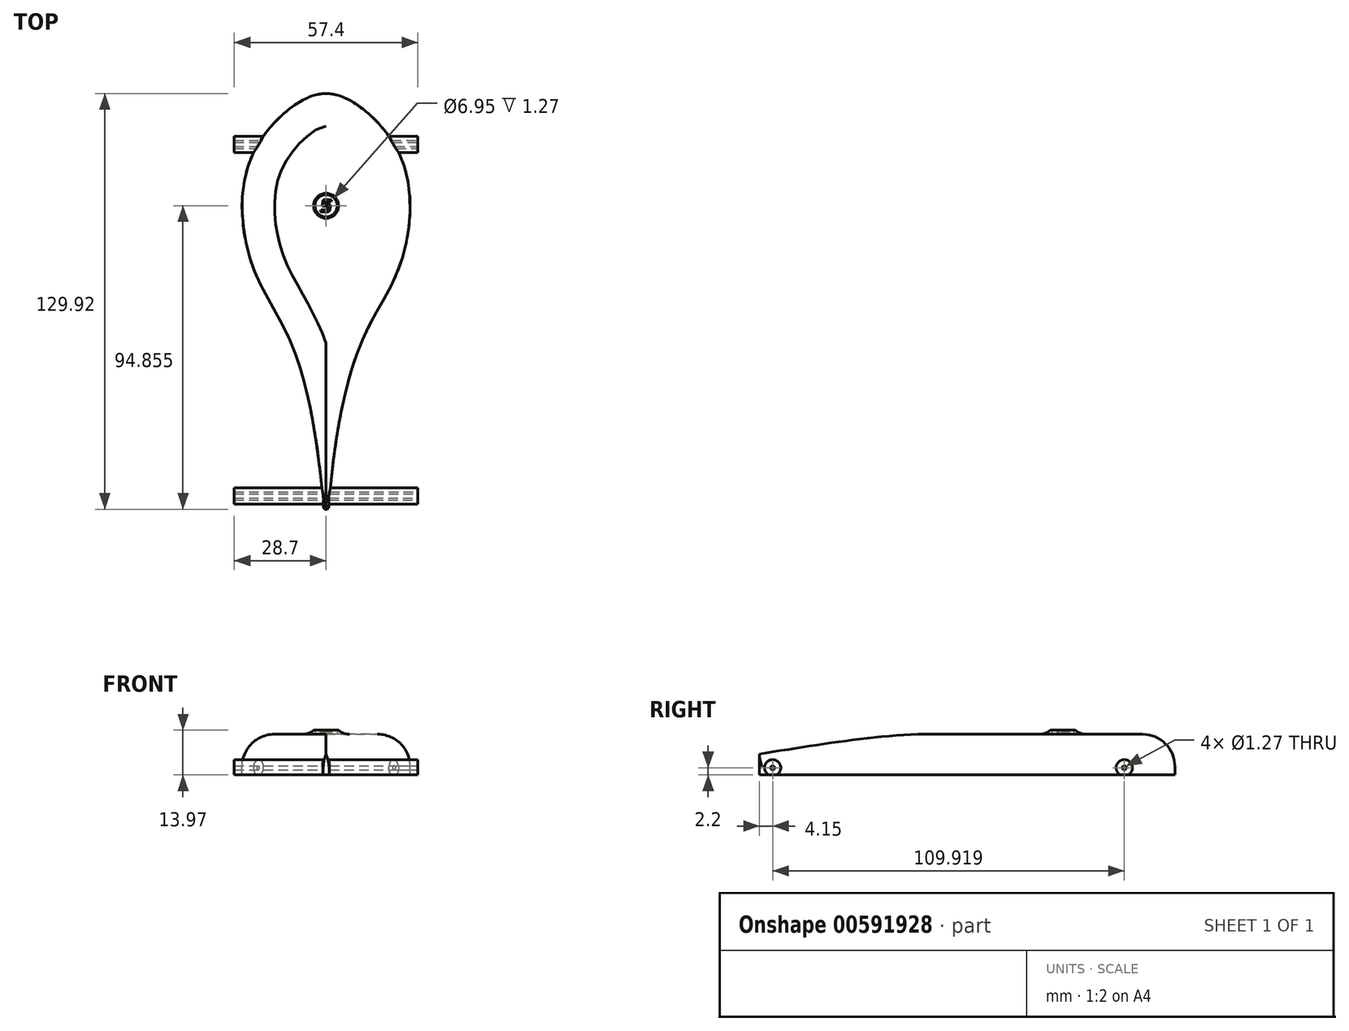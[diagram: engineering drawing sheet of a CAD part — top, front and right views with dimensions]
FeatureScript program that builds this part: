
annotation { "Feature Type Name" : "Feature", "Feature Type Description" : "" }
export const myFeature = defineFeature(function(context is Context, id is Id, definition is map)
    precondition{}
    {
        {
            var Q0;
            Q0=qCreatedBy(makeId("Top.planeOp"),FACE);
            var sketch = newSketch(context, id + "F0", { "sketchPlane" : qUnion([Q0])});
            skLineSegment(sketch, "E0", {"start": v(0, 41.15) * mm, "end": v(0, 41.15) * mm});
            skFitSpline(sketch, "E1", {"points": [v(0, 41.15) * mm, v(-11.67, 36.2) * mm, v(-24.8, 17.18) * mm, v(-22.86, -13.1) * mm, v(-9.97, -39.25) * mm, v(0, -110) * mm], "startDerivative": vector(-88.12, 0) * mm, "endDerivative": vector(1.08, -257.24) * mm});
            skLineSegment(sketch, "E2", {"start": v(0, -88.77) * mm, "end": v(0, 41.15) * mm});
            skArc(sketch, "E3", {"start": v(-0.85, -87.98) * mm, "mid": v(-0.58, -88.54) * mm, "end": v(0, -88.77) * mm});
            skSolve(sketch);
        }
        {
            var Q0;
            Q0=qSketchRegion(id+"F0",true);
            extrude(context, id + "F1", {"entities" : qUnion([Q0]), "depth" : 12.7 * mm, "offsetDistance" : 25.4 * mm});
        }
        {
            var Q0;
            Q0=qCreatedBy(makeId("Right.planeOp"),FACE);
            var sketch = newSketch(context, id + "F2", { "sketchPlane" : qUnion([Q0])});
            skArc(sketch, "E4", {"start": v(-83.35, 0) * mm, "mid": v(-84.62, 4.74) * mm, "end": v(-85.89, 0) * mm});
            skCircle(sketch, "E5", {"center": v(-84.62, 2.2) * mm, "radius": 0.64 * mm});
            skLineSegment(sketch, "E6", {"start": v(-83.35, 0) * mm, "end": v(-85.89, 0) * mm});
            skArc(sketch, "E7", {"start": v(26.57, 0) * mm, "mid": v(25.3, 4.74) * mm, "end": v(24.03, 0) * mm});
            skCircle(sketch, "E8", {"center": v(25.3, 2.2) * mm, "radius": 0.64 * mm});
            skLineSegment(sketch, "E9", {"start": v(26.57, 0) * mm, "end": v(24.03, 0) * mm});
            skSolve(sketch);
        }
        {
            var Q0;
            Q0=makeQuery(id+"F1.opExtrude","SWEPT_BODY",BODY,{"disambiguationData":[OSD([sQuery(id+"F0.wireOp",EDGE,"E1"),sQuery(id+"F0.wireOp",EDGE,"E2")])]});
            var Q1;
            Q1=makeQuery(id+"F1.opExtrude","SWEPT_FACE",FACE,{"disambiguationData":[OSD([sQuery(id+"F0.wireOp",EDGE,"E2")])]});
            mirror(context, id + "F3", {"entities" : qUnion([Q0]), "mirrorPlane" : qUnion([Q1])});
        }
        {
            var Q0;
            Q0=qSketchRegion(id+"F2",true);
            extrude(context, id + "F4", {"entities" : qUnion([Q0]), "endBound" : BoundingType.SYMMETRIC, "oppositeDirection" : true, "depth" : 57.4 * mm, "offsetDistance" : 25.4 * mm});
        }
        {
            var Q0;
            Q0=makeQuery(id+"F1.opExtrude","CAP_EDGE",EDGE,{"disambiguationData":[OSD([sQuery(id+"F0.wireOp",EDGE,"E1")])],"isStart":false});
            var Q1;
            Q1=makeQuery(id+"F3.opPattern","COPY",EDGE,{"derivedFrom":makeQuery(id+"F1.opExtrude","CAP_EDGE",EDGE,{"disambiguationData":[OSD([sQuery(id+"F0.wireOp",EDGE,"E1")])],"isStart":false}),"instanceName":"1"});
            fillet(context, id + "F5", {"entities" : qUnion([Q0, Q1]), "radius" : 10.16 * mm, "tangentPropagation" : true, "allowEdgeOverflow" : false});
        }
        {
            var Q0;
            {var subQ0=makeQuery(id+"F1.opExtrude","CAP_FACE",FACE,{"disambiguationData":[OSD([sQuery(id+"F0.wireOp",EDGE,"E1"),sQuery(id+"F0.wireOp",EDGE,"E2")])],"isStart":false});Q0=makeQuery(id+"F9.opBoolean","MERGE",FACE,{"derivedFrom":[subQ0,makeQuery(id+"F3.opPattern","COPY",FACE,{"derivedFrom":subQ0,"instanceName":"1"})]});}
            var sketch = newSketch(context, id + "F6", { "sketchPlane" : qUnion([Q0])});
            skCircle(sketch, "E10", {"center": v(0, 6.09) * mm, "radius": 3.47 * mm});
            skCircle(sketch, "E11", {"center": v(0, 6.09) * mm, "radius": 3.9 * mm});
            skSolve(sketch);
        }
        {
            var Q0;
            {var subQ0=makeQuery(id+"F1.opExtrude","CAP_FACE",FACE,{"disambiguationData":[OSD([sQuery(id+"F0.wireOp",EDGE,"E1"),sQuery(id+"F0.wireOp",EDGE,"E2")])],"isStart":false});Q0=makeQuery(id+"F9.opBoolean","MERGE",FACE,{"derivedFrom":[subQ0,makeQuery(id+"F3.opPattern","COPY",FACE,{"derivedFrom":subQ0,"instanceName":"1"})]});}
            var sketch = newSketch(context, id + "F7", { "sketchPlane" : qUnion([Q0])});
            skLineSegment(sketch, "E12", {"start": v(0.3, 4.16) * mm, "end": v(0.45, 4.17) * mm});
            skLineSegment(sketch, "E13", {"start": v(0.45, 4.17) * mm, "end": v(0.58, 4.2) * mm});
            skLineSegment(sketch, "E14", {"start": v(0.58, 4.2) * mm, "end": v(0.68, 4.22) * mm});
            skLineSegment(sketch, "E15", {"start": v(0.68, 4.22) * mm, "end": v(0.78, 4.27) * mm});
            skLineSegment(sketch, "E16", {"start": v(0.78, 4.27) * mm, "end": v(0.86, 4.31) * mm});
            skLineSegment(sketch, "E17", {"start": v(0.86, 4.31) * mm, "end": v(0.93, 4.37) * mm});
            skLineSegment(sketch, "E18", {"start": v(0.93, 4.37) * mm, "end": v(1, 4.43) * mm});
            skLineSegment(sketch, "E19", {"start": v(1, 4.43) * mm, "end": v(1.06, 4.51) * mm});
            skLineSegment(sketch, "E20", {"start": v(1.06, 4.51) * mm, "end": v(1.12, 4.62) * mm});
            skLineSegment(sketch, "E21", {"start": v(1.12, 4.62) * mm, "end": v(1.17, 4.75) * mm});
            skLineSegment(sketch, "E22", {"start": v(1.17, 4.75) * mm, "end": v(1.22, 4.9) * mm});
            skLineSegment(sketch, "E23", {"start": v(0.15, 4.8) * mm, "end": v(0.26, 4.8) * mm});
            skLineSegment(sketch, "E24", {"start": v(0.26, 4.8) * mm, "end": v(0.35, 4.83) * mm});
            skLineSegment(sketch, "E25", {"start": v(0.35, 4.83) * mm, "end": v(0.4, 4.85) * mm});
            skLineSegment(sketch, "E26", {"start": v(0.4, 4.85) * mm, "end": v(0.43, 4.87) * mm});
            skLineSegment(sketch, "E27", {"start": v(0.43, 4.87) * mm, "end": v(0.45, 4.9) * mm});
            skLineSegment(sketch, "E28", {"start": v(0.45, 4.9) * mm, "end": v(0.47, 4.94) * mm});
            skLineSegment(sketch, "E29", {"start": v(0.53, 5.9) * mm, "end": v(0.58, 5.88) * mm});
            skLineSegment(sketch, "E30", {"start": v(0.58, 5.88) * mm, "end": v(0.62, 5.85) * mm});
            skLineSegment(sketch, "E31", {"start": v(0.62, 5.85) * mm, "end": v(0.63, 5.81) * mm});
            skLineSegment(sketch, "E32", {"start": v(0.63, 5.81) * mm, "end": v(0.63, 5.76) * mm});
            skLineSegment(sketch, "E33", {"start": v(0.9, 6.54) * mm, "end": v(0.95, 6.54) * mm});
            skLineSegment(sketch, "E34", {"start": v(0.95, 6.54) * mm, "end": v(1.02, 6.52) * mm});
            skLineSegment(sketch, "E35", {"start": v(1.02, 6.52) * mm, "end": v(1.08, 6.5) * mm});
            skLineSegment(sketch, "E36", {"start": v(1.08, 6.5) * mm, "end": v(1.15, 6.47) * mm});
            skLineSegment(sketch, "E37", {"start": v(1.15, 6.47) * mm, "end": v(1.23, 6.42) * mm});
            skLineSegment(sketch, "E38", {"start": v(1.23, 6.42) * mm, "end": v(1.3, 6.36) * mm});
            skLineSegment(sketch, "E39", {"start": v(1.3, 6.36) * mm, "end": v(1.34, 6.28) * mm});
            skLineSegment(sketch, "E40", {"start": v(1.34, 6.28) * mm, "end": v(1.39, 6.17) * mm});
            skLineSegment(sketch, "E41", {"start": v(1.39, 6.17) * mm, "end": v(1.4, 6.05) * mm});
            skLineSegment(sketch, "E42", {"start": v(1.4, 6.05) * mm, "end": v(1.41, 5.94) * mm});
            skLineSegment(sketch, "E43", {"start": v(1.41, 5.94) * mm, "end": v(1.4, 5.84) * mm});
            skLineSegment(sketch, "E44", {"start": v(-1.24, 6.32) * mm, "end": v(-1.24, 6.22) * mm});
            skLineSegment(sketch, "E45", {"start": v(-1.24, 6.22) * mm, "end": v(-1.2, 6.13) * mm});
            skLineSegment(sketch, "E46", {"start": v(-1.2, 6.13) * mm, "end": v(-1.15, 6.05) * mm});
            skLineSegment(sketch, "E47", {"start": v(-1.15, 6.05) * mm, "end": v(-1.09, 5.99) * mm});
            skLineSegment(sketch, "E48", {"start": v(-1.09, 5.99) * mm, "end": v(-1.01, 5.94) * mm});
            skLineSegment(sketch, "E49", {"start": v(-1.01, 5.94) * mm, "end": v(-0.92, 5.9) * mm});
            skLineSegment(sketch, "E50", {"start": v(-0.92, 5.9) * mm, "end": v(-0.8, 5.9) * mm});
            skLineSegment(sketch, "E51", {"start": v(-0.45, 6.78) * mm, "end": v(-0.46, 6.73) * mm});
            skLineSegment(sketch, "E52", {"start": v(-0.46, 6.73) * mm, "end": v(-0.46, 6.67) * mm});
            skLineSegment(sketch, "E53", {"start": v(-0.46, 6.67) * mm, "end": v(-0.45, 6.62) * mm});
            skLineSegment(sketch, "E54", {"start": v(-0.45, 6.62) * mm, "end": v(-0.43, 6.59) * mm});
            skLineSegment(sketch, "E55", {"start": v(-0.43, 6.59) * mm, "end": v(-0.4, 6.56) * mm});
            skLineSegment(sketch, "E56", {"start": v(-0.4, 6.56) * mm, "end": v(-0.36, 6.55) * mm});
            skLineSegment(sketch, "E57", {"start": v(-0.36, 6.55) * mm, "end": v(-0.32, 6.54) * mm});
            skLineSegment(sketch, "E58", {"start": v(-1.1, 7.3) * mm, "end": v(-1.1, 7.35) * mm});
            skLineSegment(sketch, "E59", {"start": v(-1.1, 7.35) * mm, "end": v(-1.07, 7.42) * mm});
            skLineSegment(sketch, "E60", {"start": v(-1.07, 7.42) * mm, "end": v(-1.04, 7.51) * mm});
            skLineSegment(sketch, "E61", {"start": v(-1.04, 7.51) * mm, "end": v(-1, 7.6) * mm});
            skLineSegment(sketch, "E62", {"start": v(-1, 7.6) * mm, "end": v(-0.95, 7.7) * mm});
            skLineSegment(sketch, "E63", {"start": v(-0.95, 7.7) * mm, "end": v(-0.89, 7.8) * mm});
            skLineSegment(sketch, "E64", {"start": v(-0.89, 7.8) * mm, "end": v(-0.81, 7.87) * mm});
            skLineSegment(sketch, "E65", {"start": v(-0.81, 7.87) * mm, "end": v(-0.72, 7.93) * mm});
            skLineSegment(sketch, "E66", {"start": v(-0.72, 7.93) * mm, "end": v(-0.63, 7.98) * mm});
            skLineSegment(sketch, "E67", {"start": v(-0.63, 7.98) * mm, "end": v(-0.54, 8) * mm});
            skLineSegment(sketch, "E68", {"start": v(-0.54, 8) * mm, "end": v(-0.47, 8.02) * mm});
            skLineSegment(sketch, "E69", {"start": v(-0.47, 8.02) * mm, "end": v(-0.41, 8.02) * mm});
            skLineSegment(sketch, "E70", {"start": v(0.53, 5.9) * mm, "end": v(-0.8, 5.9) * mm});
            skLineSegment(sketch, "E71", {"start": v(-1.63, 4.8) * mm, "end": v(0.15, 4.8) * mm});
            skLineSegment(sketch, "E72", {"start": v(-1.78, 4.16) * mm, "end": v(-1.63, 4.8) * mm});
            skLineSegment(sketch, "E73", {"start": v(0.3, 4.16) * mm, "end": v(-1.78, 4.16) * mm});
            skLineSegment(sketch, "E74", {"start": v(-0.32, 6.54) * mm, "end": v(0.9, 6.54) * mm});
            skLineSegment(sketch, "E75", {"start": v(-0.39, 7.25) * mm, "end": v(-0.45, 6.78) * mm});
            skLineSegment(sketch, "E76", {"start": v(1.67, 8.02) * mm, "end": v(-0.41, 8.02) * mm});
            skLineSegment(sketch, "E77", {"start": v(1.51, 7.4) * mm, "end": v(1.67, 8.02) * mm});
            skLineSegment(sketch, "E78", {"start": v(-0.1, 7.4) * mm, "end": v(1.51, 7.4) * mm});
            skLineSegment(sketch, "E79", {"start": v(-1.1, 7.3) * mm, "end": v(-1.24, 6.32) * mm});
            skLineSegment(sketch, "E80", {"start": v(-0.39, 7.25) * mm, "end": v(-0.36, 7.3) * mm});
            skLineSegment(sketch, "E81", {"start": v(-0.36, 7.3) * mm, "end": v(-0.32, 7.35) * mm});
            skLineSegment(sketch, "E82", {"start": v(-0.32, 7.35) * mm, "end": v(-0.26, 7.38) * mm});
            skLineSegment(sketch, "E83", {"start": v(-0.26, 7.38) * mm, "end": v(-0.18, 7.4) * mm});
            skLineSegment(sketch, "E84", {"start": v(-0.18, 7.4) * mm, "end": v(-0.1, 7.4) * mm});
            skLineSegment(sketch, "E85", {"start": v(0.63, 5.76) * mm, "end": v(0.47, 4.94) * mm});
            skLineSegment(sketch, "E86", {"start": v(1.4, 5.84) * mm, "end": v(1.22, 4.9) * mm});
            skSolve(sketch);
        }
        {
            var Q0;
            Q0 = qSketchRegion(id + "F7", true);
            var Q1;
            Q1 = qSketchRegion(id + "F6", true);
            var Q2;
            Q2=sQuery(id+"F7.wireOp",EDGE,"E12");
            var Q3;
            Q3=sQuery(id+"F7.wireOp",EDGE,"E13");
            var Q4;
            Q4=sQuery(id+"F7.wireOp",EDGE,"E14");
            var Q5;
            Q5=sQuery(id+"F7.wireOp",EDGE,"E15");
            var Q6;
            Q6=sQuery(id+"F7.wireOp",EDGE,"E16");
            var Q7;
            Q7=sQuery(id+"F7.wireOp",EDGE,"E17");
            var Q8;
            Q8=sQuery(id+"F7.wireOp",EDGE,"E18");
            var Q9;
            Q9=sQuery(id+"F7.wireOp",EDGE,"E19");
            var Q10;
            Q10=sQuery(id+"F7.wireOp",EDGE,"E20");
            var Q11;
            Q11=sQuery(id+"F7.wireOp",EDGE,"E21");
            var Q12;
            Q12=sQuery(id+"F7.wireOp",EDGE,"E22");
            var Q13;
            Q13=sQuery(id+"F7.wireOp",EDGE,"E23");
            var Q14;
            Q14=sQuery(id+"F7.wireOp",EDGE,"E24");
            var Q15;
            Q15=sQuery(id+"F7.wireOp",EDGE,"E25");
            var Q16;
            Q16=sQuery(id+"F7.wireOp",EDGE,"E26");
            var Q17;
            Q17=sQuery(id+"F7.wireOp",EDGE,"E27");
            var Q18;
            Q18=sQuery(id+"F7.wireOp",EDGE,"E28");
            var Q19;
            Q19=sQuery(id+"F7.wireOp",EDGE,"E29");
            var Q20;
            Q20=sQuery(id+"F7.wireOp",EDGE,"E30");
            var Q21;
            Q21=sQuery(id+"F7.wireOp",EDGE,"E31");
            var Q22;
            Q22=sQuery(id+"F7.wireOp",EDGE,"E32");
            var Q23;
            Q23=sQuery(id+"F7.wireOp",EDGE,"E33");
            var Q24;
            Q24=sQuery(id+"F7.wireOp",EDGE,"E34");
            var Q25;
            Q25=sQuery(id+"F7.wireOp",EDGE,"E35");
            var Q26;
            Q26=sQuery(id+"F7.wireOp",EDGE,"E36");
            var Q27;
            Q27=sQuery(id+"F7.wireOp",EDGE,"E37");
            var Q28;
            Q28=sQuery(id+"F7.wireOp",EDGE,"E38");
            var Q29;
            Q29=sQuery(id+"F7.wireOp",EDGE,"E39");
            var Q30;
            Q30=sQuery(id+"F7.wireOp",EDGE,"E40");
            var Q31;
            Q31=sQuery(id+"F7.wireOp",EDGE,"E41");
            var Q32;
            Q32=sQuery(id+"F7.wireOp",EDGE,"E42");
            var Q33;
            Q33=sQuery(id+"F7.wireOp",EDGE,"E43");
            var Q34;
            Q34=sQuery(id+"F7.wireOp",EDGE,"E44");
            var Q35;
            Q35=sQuery(id+"F7.wireOp",EDGE,"E45");
            var Q36;
            Q36=sQuery(id+"F7.wireOp",EDGE,"E46");
            var Q37;
            Q37=sQuery(id+"F7.wireOp",EDGE,"E47");
            var Q38;
            Q38=sQuery(id+"F7.wireOp",EDGE,"E48");
            var Q39;
            Q39=sQuery(id+"F7.wireOp",EDGE,"E49");
            var Q40;
            Q40=sQuery(id+"F7.wireOp",EDGE,"E50");
            var Q41;
            Q41=sQuery(id+"F7.wireOp",EDGE,"E51");
            var Q42;
            Q42=sQuery(id+"F7.wireOp",EDGE,"E52");
            var Q43;
            Q43=sQuery(id+"F7.wireOp",EDGE,"E53");
            var Q44;
            Q44=sQuery(id+"F7.wireOp",EDGE,"E54");
            var Q45;
            Q45=sQuery(id+"F7.wireOp",EDGE,"E55");
            var Q46;
            Q46=sQuery(id+"F7.wireOp",EDGE,"E56");
            var Q47;
            Q47=sQuery(id+"F7.wireOp",EDGE,"E57");
            var Q48;
            Q48=sQuery(id+"F7.wireOp",EDGE,"E58");
            var Q49;
            Q49=sQuery(id+"F7.wireOp",EDGE,"E59");
            var Q50;
            Q50=sQuery(id+"F7.wireOp",EDGE,"E60");
            var Q51;
            Q51=sQuery(id+"F7.wireOp",EDGE,"E61");
            var Q52;
            Q52=sQuery(id+"F7.wireOp",EDGE,"E62");
            var Q53;
            Q53=sQuery(id+"F7.wireOp",EDGE,"E63");
            var Q54;
            Q54=sQuery(id+"F7.wireOp",EDGE,"E64");
            var Q55;
            Q55=sQuery(id+"F7.wireOp",EDGE,"E65");
            var Q56;
            Q56=sQuery(id+"F7.wireOp",EDGE,"E66");
            var Q57;
            Q57=sQuery(id+"F7.wireOp",EDGE,"E67");
            var Q58;
            Q58=sQuery(id+"F7.wireOp",EDGE,"E68");
            var Q59;
            Q59=sQuery(id+"F7.wireOp",EDGE,"E69");
            var Q60;
            Q60=sQuery(id+"F7.wireOp",EDGE,"E70");
            var Q61;
            Q61=sQuery(id+"F7.wireOp",EDGE,"E71");
            var Q62;
            Q62=sQuery(id+"F7.wireOp",EDGE,"E72");
            var Q63;
            Q63=sQuery(id+"F7.wireOp",EDGE,"E73");
            var Q64;
            Q64=sQuery(id+"F7.wireOp",EDGE,"E74");
            var Q65;
            Q65=sQuery(id+"F7.wireOp",EDGE,"E75");
            var Q66;
            Q66=sQuery(id+"F7.wireOp",EDGE,"E76");
            var Q67;
            Q67=sQuery(id+"F7.wireOp",EDGE,"E77");
            var Q68;
            Q68=sQuery(id+"F7.wireOp",EDGE,"E78");
            var Q69;
            Q69=sQuery(id+"F7.wireOp",EDGE,"E79");
            var Q70;
            Q70=sQuery(id+"F7.wireOp",EDGE,"E80");
            var Q71;
            Q71=sQuery(id+"F7.wireOp",EDGE,"E81");
            var Q72;
            Q72=sQuery(id+"F7.wireOp",EDGE,"E82");
            var Q73;
            Q73=sQuery(id+"F7.wireOp",EDGE,"E83");
            var Q74;
            Q74=sQuery(id+"F7.wireOp",EDGE,"E84");
            var Q75;
            Q75=sQuery(id+"F7.wireOp",EDGE,"E85");
            var Q76;
            Q76=sQuery(id+"F7.wireOp",EDGE,"E86");
            extrude(context, id + "F8", {"entities" : qUnion([Q0, Q1]), "surfaceEntities" : qUnion([Q2, Q3, Q4, Q5, Q6, Q7, Q8, Q9, Q10, Q11, Q12, Q13, Q14, Q15, Q16, Q17, Q18, Q19, Q20, Q21, Q22, Q23, Q24, Q25, Q26, Q27, Q28, Q29, Q30, Q31, Q32, Q33, Q34, Q35, Q36, Q37, Q38, Q39, Q40, Q41, Q42, Q43, Q44, Q45, Q46, Q47, Q48, Q49, Q50, Q51, Q52, Q53, Q54, Q55, Q56, Q57, Q58, Q59, Q60, Q61, Q62, Q63, Q64, Q65, Q66, Q67, Q68, Q69, Q70, Q71, Q72, Q73, Q74, Q75, Q76]), "depth" : 1.27 * mm, "offsetDistance" : 25.4 * mm});
        }
        {
            var Q0;
            Q0=makeQuery(id+"F4.opExtrude","SWEPT_BODY",BODY,{"disambiguationData":[OSD([sQuery(id+"F2.wireOp",EDGE,"E4"),sQuery(id+"F2.wireOp",EDGE,"E5"),sQuery(id+"F2.wireOp",EDGE,"E6")])]});
            var Q1;
            Q1=makeQuery(id+"F1.opExtrude","SWEPT_BODY",BODY,{"disambiguationData":[OSD([sQuery(id+"F0.wireOp",EDGE,"E1"),sQuery(id+"F0.wireOp",EDGE,"E2")])]});
            var Q2;
            Q2=makeQuery(id+"F4.opExtrude","SWEPT_BODY",BODY,{"disambiguationData":[OSD([sQuery(id+"F2.wireOp",EDGE,"E7"),sQuery(id+"F2.wireOp",EDGE,"E8"),sQuery(id+"F2.wireOp",EDGE,"E9")])]});
            var Q3;
            Q3=makeQuery(id+"F3.opPattern","COPY",BODY,{"derivedFrom":makeQuery(id+"F1.opExtrude","SWEPT_BODY",BODY,{"disambiguationData":[OSD([sQuery(id+"F0.wireOp",EDGE,"E1"),sQuery(id+"F0.wireOp",EDGE,"E2")])]}),"instanceName":"1"});
            var Q4;
            Q4=makeQuery(id+"F8.opExtrude","SWEPT_BODY",BODY,{"disambiguationData":[OSD([sQuery(id+"F6.wireOp",EDGE,"E10"),sQuery(id+"F6.wireOp",EDGE,"E11")])]});
            var Q5;
            Q5=makeQuery(id+"F8.opExtrude","SWEPT_BODY",BODY,{"disambiguationData":[OSD([sQuery(id+"F7.wireOp",EDGE,"E12"),sQuery(id+"F7.wireOp",EDGE,"E13"),sQuery(id+"F7.wireOp",EDGE,"E14"),sQuery(id+"F7.wireOp",EDGE,"E15"),sQuery(id+"F7.wireOp",EDGE,"E16"),sQuery(id+"F7.wireOp",EDGE,"E17"),sQuery(id+"F7.wireOp",EDGE,"E18"),sQuery(id+"F7.wireOp",EDGE,"E19"),sQuery(id+"F7.wireOp",EDGE,"E20"),sQuery(id+"F7.wireOp",EDGE,"E21"),sQuery(id+"F7.wireOp",EDGE,"E22"),sQuery(id+"F7.wireOp",EDGE,"E23"),sQuery(id+"F7.wireOp",EDGE,"E24"),sQuery(id+"F7.wireOp",EDGE,"E25"),sQuery(id+"F7.wireOp",EDGE,"E26"),sQuery(id+"F7.wireOp",EDGE,"E27"),sQuery(id+"F7.wireOp",EDGE,"E28"),sQuery(id+"F7.wireOp",EDGE,"E29"),sQuery(id+"F7.wireOp",EDGE,"E30"),sQuery(id+"F7.wireOp",EDGE,"E31"),sQuery(id+"F7.wireOp",EDGE,"E32"),sQuery(id+"F7.wireOp",EDGE,"E33"),sQuery(id+"F7.wireOp",EDGE,"E34"),sQuery(id+"F7.wireOp",EDGE,"E35"),sQuery(id+"F7.wireOp",EDGE,"E36"),sQuery(id+"F7.wireOp",EDGE,"E37"),sQuery(id+"F7.wireOp",EDGE,"E38"),sQuery(id+"F7.wireOp",EDGE,"E39"),sQuery(id+"F7.wireOp",EDGE,"E40"),sQuery(id+"F7.wireOp",EDGE,"E41"),sQuery(id+"F7.wireOp",EDGE,"E42"),sQuery(id+"F7.wireOp",EDGE,"E43"),sQuery(id+"F7.wireOp",EDGE,"E44"),sQuery(id+"F7.wireOp",EDGE,"E45"),sQuery(id+"F7.wireOp",EDGE,"E46"),sQuery(id+"F7.wireOp",EDGE,"E47"),sQuery(id+"F7.wireOp",EDGE,"E48"),sQuery(id+"F7.wireOp",EDGE,"E49"),sQuery(id+"F7.wireOp",EDGE,"E50"),sQuery(id+"F7.wireOp",EDGE,"E51"),sQuery(id+"F7.wireOp",EDGE,"E52"),sQuery(id+"F7.wireOp",EDGE,"E53"),sQuery(id+"F7.wireOp",EDGE,"E54"),sQuery(id+"F7.wireOp",EDGE,"E55"),sQuery(id+"F7.wireOp",EDGE,"E56"),sQuery(id+"F7.wireOp",EDGE,"E57"),sQuery(id+"F7.wireOp",EDGE,"E58"),sQuery(id+"F7.wireOp",EDGE,"E59"),sQuery(id+"F7.wireOp",EDGE,"E60"),sQuery(id+"F7.wireOp",EDGE,"E61"),sQuery(id+"F7.wireOp",EDGE,"E62"),sQuery(id+"F7.wireOp",EDGE,"E63"),sQuery(id+"F7.wireOp",EDGE,"E64"),sQuery(id+"F7.wireOp",EDGE,"E65"),sQuery(id+"F7.wireOp",EDGE,"E66"),sQuery(id+"F7.wireOp",EDGE,"E67"),sQuery(id+"F7.wireOp",EDGE,"E68"),sQuery(id+"F7.wireOp",EDGE,"E69"),sQuery(id+"F7.wireOp",EDGE,"E70"),sQuery(id+"F7.wireOp",EDGE,"E71"),sQuery(id+"F7.wireOp",EDGE,"E72"),sQuery(id+"F7.wireOp",EDGE,"E73"),sQuery(id+"F7.wireOp",EDGE,"E74"),sQuery(id+"F7.wireOp",EDGE,"E75"),sQuery(id+"F7.wireOp",EDGE,"E76"),sQuery(id+"F7.wireOp",EDGE,"E77"),sQuery(id+"F7.wireOp",EDGE,"E78"),sQuery(id+"F7.wireOp",EDGE,"E79"),sQuery(id+"F7.wireOp",EDGE,"E80"),sQuery(id+"F7.wireOp",EDGE,"E81"),sQuery(id+"F7.wireOp",EDGE,"E82"),sQuery(id+"F7.wireOp",EDGE,"E83"),sQuery(id+"F7.wireOp",EDGE,"E84"),sQuery(id+"F7.wireOp",EDGE,"E85"),sQuery(id+"F7.wireOp",EDGE,"E86")])]});
            booleanBodies(context, id + "F9", {"operationType" : BooleanOperationType.UNION, "tools" : qUnion([Q0, Q1, Q2, Q3, Q4, Q5])});
        }
        {
            var Q0;
            {var subQ0=makeQuery(id+"F1.opExtrude","CAP_FACE",FACE,{"disambiguationData":[OSD([sQuery(id+"F0.wireOp",EDGE,"E1"),sQuery(id+"F0.wireOp",EDGE,"E2")])],"isStart":false});var subQ1=makeQuery(id+"F3.opPattern","COPY",FACE,{"derivedFrom":subQ0,"instanceName":"1"});Q0=makeQuery(id+"F9.opBoolean","INTERSECT",EDGE,{"disambiguationData":[topologyDisambiguationEdgeConnected([makeQuery(id+"F8.opExtrude","SWEPT_FACE",FACE,{"disambiguationData":[OSD([sQuery(id+"F6.wireOp",EDGE,"E11")])]})])],"derivedFrom":[subQ0,subQ1]});}
            fillet(context, id + "F10", {"entities" : qUnion([Q0]), "radius" : 5.08 * mm, "tangentPropagation" : true, "allowEdgeOverflow" : false});
        }
    });
